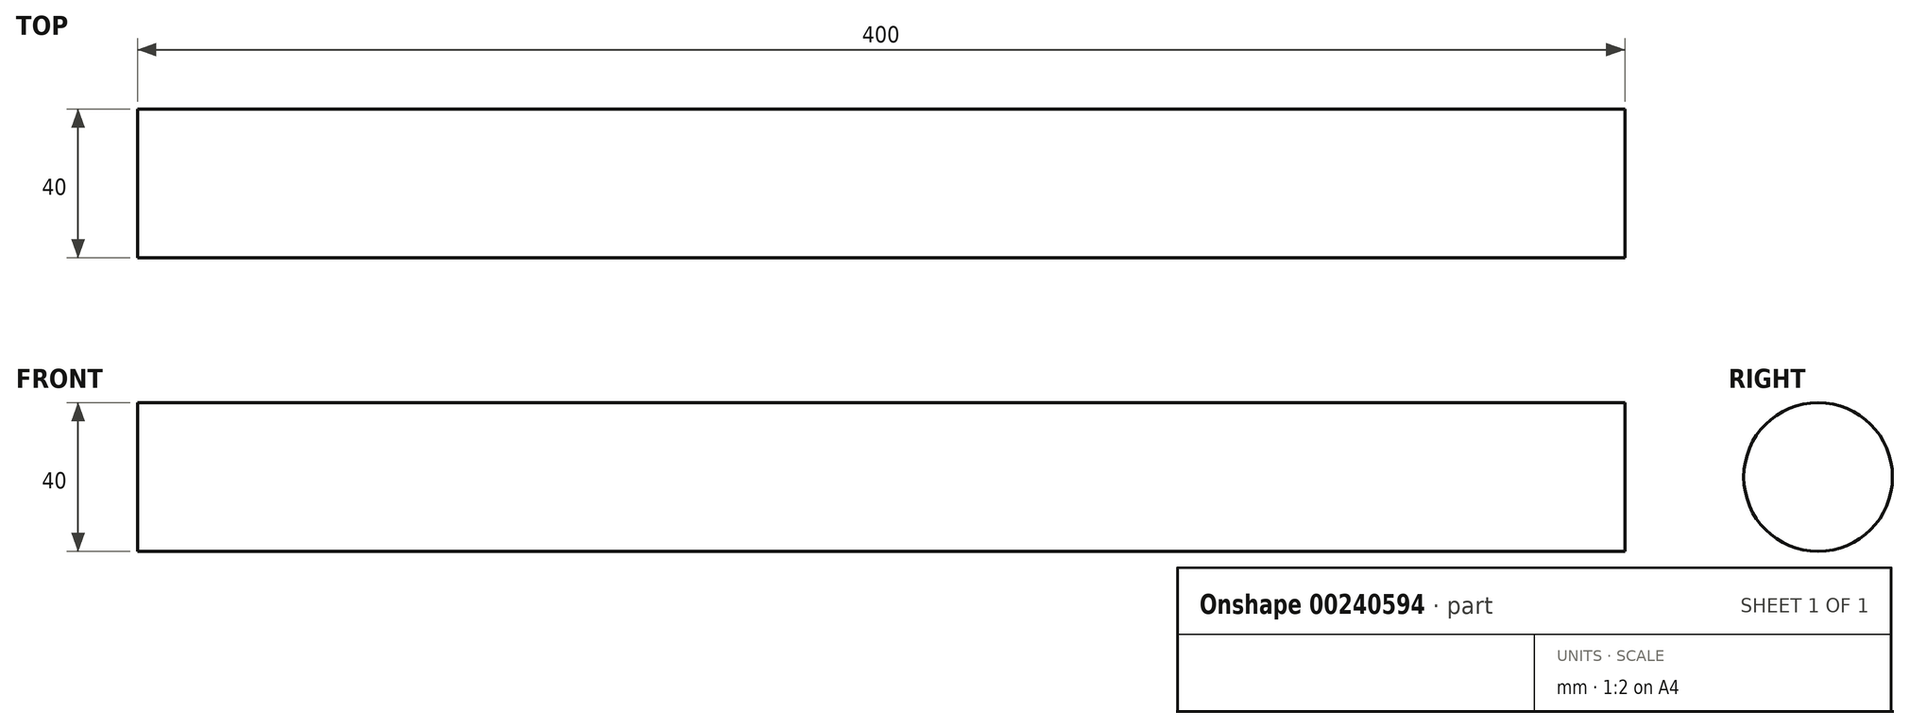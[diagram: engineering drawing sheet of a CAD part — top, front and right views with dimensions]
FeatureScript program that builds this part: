
annotation { "Feature Type Name" : "Feature", "Feature Type Description" : "" }
export const myFeature = defineFeature(function(context is Context, id is Id, definition is map)
    precondition{}
    {
        {
            var Q0;
            Q0=qCreatedBy(makeId("Right.planeOp"),FACE);
            var sketch = newSketch(context, id + "F0", { "sketchPlane" : qUnion([Q0])});
            skCircle(sketch, "E0", {"center": v(0, 0) * mm, "radius": 20 * mm});
            skSolve(sketch);
        }
        {
            var Q0;
            Q0 = qSketchRegion(id + "F0", true);
            extrude(context, id + "F1", {"entities" : qUnion([Q0]), "depth" : 400 * mm, "offsetDistance" : 25 * mm});
        }
    });
